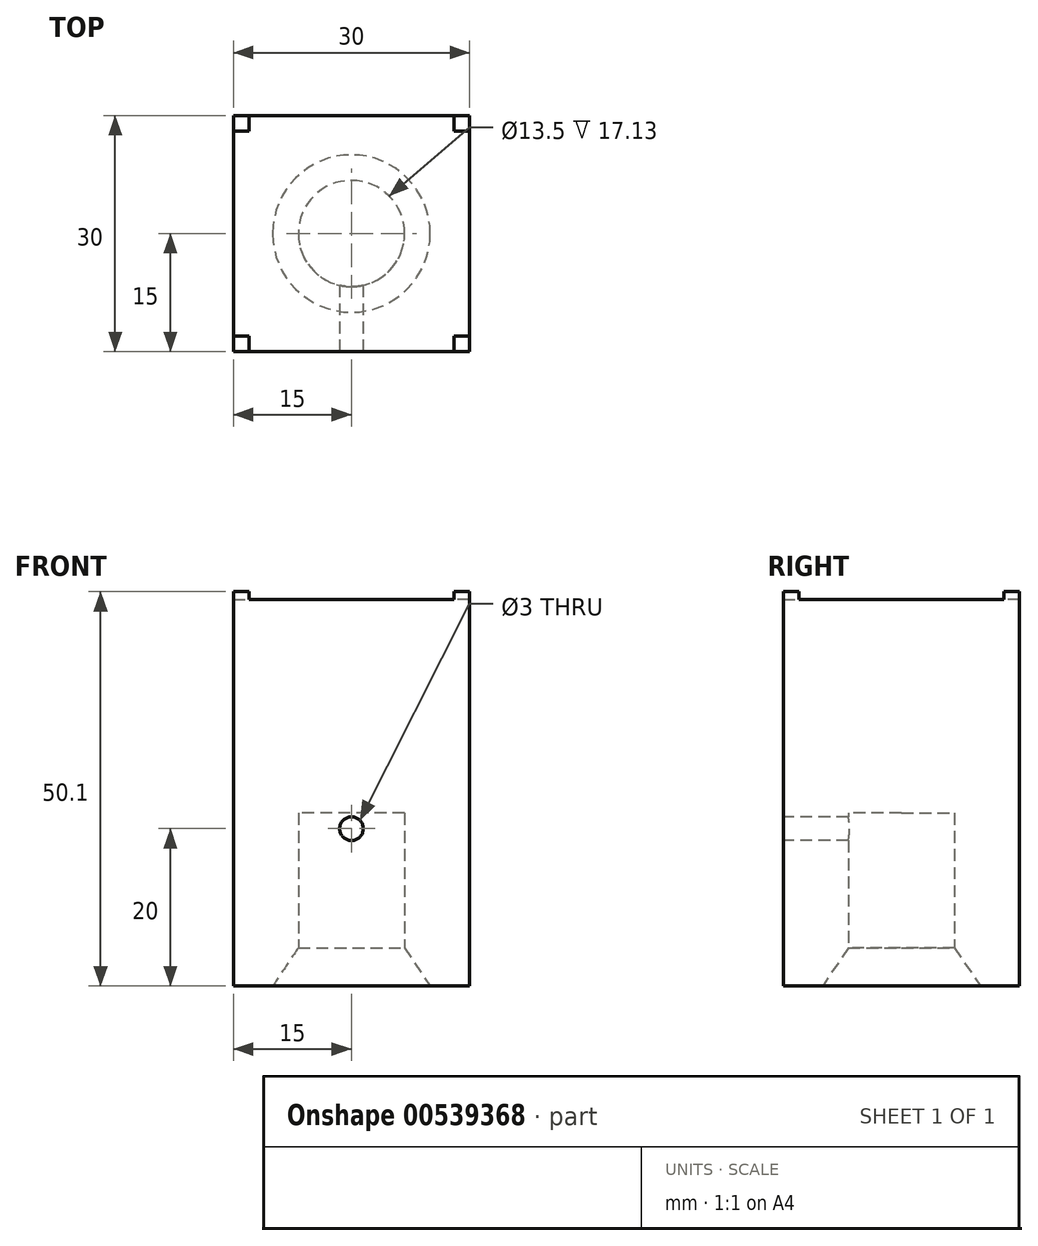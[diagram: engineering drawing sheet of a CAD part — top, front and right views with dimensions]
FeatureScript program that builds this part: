
annotation { "Feature Type Name" : "Feature", "Feature Type Description" : "" }
export const myFeature = defineFeature(function(context is Context, id is Id, definition is map)
    precondition{}
    {
        {
            var Q0;
            Q0=qCreatedBy(makeId("Top.planeOp"),FACE);
            var sketch = newSketch(context, id + "F0", { "sketchPlane" : qUnion([Q0])});
            skLineSegment(sketch, "E0.bottom", {"start": v(-15, 15) * mm, "end": v(15, 15) * mm});
            skLineSegment(sketch, "E0.top", {"start": v(-15, -15) * mm, "end": v(15, -15) * mm});
            skLineSegment(sketch, "E0.left", {"start": v(-15, 15) * mm, "end": v(-15, -15) * mm});
            skLineSegment(sketch, "E0.right", {"start": v(15, 15) * mm, "end": v(15, -15) * mm});
            skSolve(sketch);
        }
        {
            var Q0;
            Q0=qSketchRegion(id+"F0",true);
            extrude(context, id + "F1", {"entities" : qUnion([Q0]), "depth" : 49.1 * mm, "offsetDistance" : 25 * mm});
        }
        {
            var Q0;
            Q0=qCreatedBy(makeId("Top.planeOp"),FACE);
            var sketch = newSketch(context, id + "F2", { "sketchPlane" : qUnion([Q0])});
            skCircle(sketch, "E1", {"center": v(0, 0) * mm, "radius": 6.75 * mm});
            skSolve(sketch);
        }
        {
            var Q0;
            Q0=qSketchRegion(id+"F2",true);
            extrude(context, id + "F3", {"entities" : qUnion([Q0]), "operationType" : NewBodyOperationType.REMOVE, "depth" : 22 * mm, "offsetDistance" : 25 * mm});
        }
        {
            var Q0;
            Q0=makeQuery(id+"F1.opExtrude","CAP_FACE",FACE,{"disambiguationData":[OSD([sQuery(id+"F0.wireOp",EDGE,"E0.bottom"),sQuery(id+"F0.wireOp",EDGE,"E0.top"),sQuery(id+"F0.wireOp",EDGE,"E0.left"),sQuery(id+"F0.wireOp",EDGE,"E0.right")])],"isStart":false});
            var sketch = newSketch(context, id + "F4", { "sketchPlane" : qUnion([Q0])});
            skLineSegment(sketch, "E2.bottom", {"start": v(15, 15) * mm, "end": v(13, 15) * mm});
            skLineSegment(sketch, "E2.top", {"start": v(15, 13) * mm, "end": v(13, 13) * mm});
            skLineSegment(sketch, "E2.left", {"start": v(15, 15) * mm, "end": v(15, 13) * mm});
            skLineSegment(sketch, "E2.right", {"start": v(13, 15) * mm, "end": v(13, 13) * mm});
            skLineSegment(sketch, "E3.bottom", {"start": v(15, -15) * mm, "end": v(13, -15) * mm});
            skLineSegment(sketch, "E3.top", {"start": v(15, -13) * mm, "end": v(13, -13) * mm});
            skLineSegment(sketch, "E3.left", {"start": v(15, -15) * mm, "end": v(15, -13) * mm});
            skLineSegment(sketch, "E3.right", {"start": v(13, -15) * mm, "end": v(13, -13) * mm});
            skLineSegment(sketch, "E4.bottom", {"start": v(-15, -15) * mm, "end": v(-13, -15) * mm});
            skLineSegment(sketch, "E4.top", {"start": v(-15, -13) * mm, "end": v(-13, -13) * mm});
            skLineSegment(sketch, "E4.left", {"start": v(-15, -15) * mm, "end": v(-15, -13) * mm});
            skLineSegment(sketch, "E4.right", {"start": v(-13, -15) * mm, "end": v(-13, -13) * mm});
            skLineSegment(sketch, "E5.bottom", {"start": v(-15, 15) * mm, "end": v(-13, 15) * mm});
            skLineSegment(sketch, "E5.top", {"start": v(-15, 13) * mm, "end": v(-13, 13) * mm});
            skLineSegment(sketch, "E5.left", {"start": v(-15, 15) * mm, "end": v(-15, 13) * mm});
            skLineSegment(sketch, "E5.right", {"start": v(-13, 15) * mm, "end": v(-13, 13) * mm});
            skSolve(sketch);
        }
        {
            var Q0;
            Q0=qSketchRegion(id+"F4",true);
            extrude(context, id + "F5", {"entities" : qUnion([Q0]), "operationType" : NewBodyOperationType.ADD, "depth" : 1 * mm, "offsetDistance" : 25 * mm});
        }
        {
            var Q0;
            Q0=qCreatedBy(makeId("Front.planeOp"),FACE);
            var sketch = newSketch(context, id + "F6", { "sketchPlane" : qUnion([Q0])});
            skLineSegment(sketch, "E6", {"start": v(0, 0) * mm, "end": v(0, 14.98) * mm});
            skLineSegment(sketch, "E7", {"start": v(0, 14.98) * mm, "end": v(10, 0) * mm});
            skLineSegment(sketch, "E8", {"start": v(10, 0) * mm, "end": v(-10, 0) * mm});
            skLineSegment(sketch, "E9", {"start": v(0, 14.98) * mm, "end": v(0, 0) * mm});
            skLineSegment(sketch, "E10", {"start": v(10, 0) * mm, "end": v(0, 0) * mm});
            skSolve(sketch);
        }
        {
            var Q0;
            Q0=qSketchRegion(id+"F6",true);
            var Q1;
            Q1=sQuery(id+"F6.wireOp",EDGE,"E9");
            revolve(context, id + "F7", {"operationType" : NewBodyOperationType.REMOVE, "entities" : qUnion([Q0]), "axis" : qUnion([Q1]), "revolveType" : RevolveType.FULL});
        }
        {
            var Q0;
            Q0=makeQuery(id+"F5.boolean.opBoolean","MERGE",FACE,{"derivedFrom":[makeQuery(id+"F1.opExtrude","SWEPT_FACE",FACE,{"disambiguationData":[OSD([sQuery(id+"F0.wireOp",EDGE,"E0.top")])]}),makeQuery(id+"F5.opExtrude","SWEPT_FACE",FACE,{"disambiguationData":[OSD([sQuery(id+"F4.wireOp",EDGE,"E3.bottom")])]}),makeQuery(id+"F5.opExtrude","SWEPT_FACE",FACE,{"disambiguationData":[OSD([sQuery(id+"F4.wireOp",EDGE,"E4.bottom")])]})]});
            var sketch = newSketch(context, id + "F8", { "sketchPlane" : qUnion([Q0])});
            skCircle(sketch, "E11", {"center": v(0, 20) * mm, "radius": 1.5 * mm});
            skSolve(sketch);
        }
        {
            var Q0;
            Q0=qSketchRegion(id+"F8",true);
            extrude(context, id + "F9", {"entities" : qUnion([Q0]), "operationType" : NewBodyOperationType.REMOVE, "endBound" : BoundingType.UP_TO_NEXT, "oppositeDirection" : true, "depth" : 25 * mm, "offsetDistance" : 25 * mm});
        }
    });
